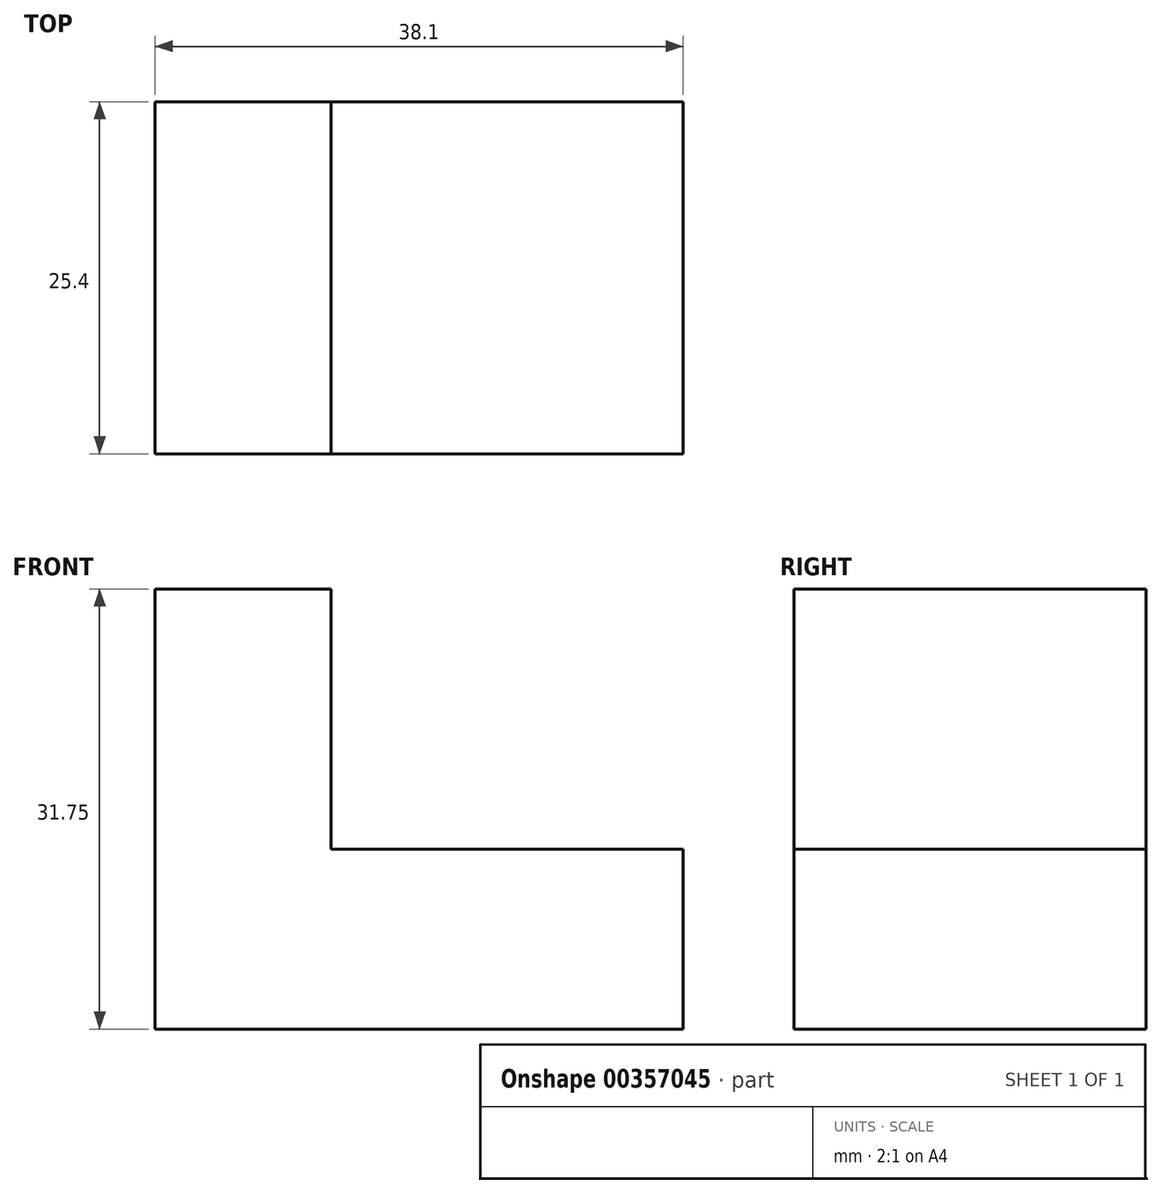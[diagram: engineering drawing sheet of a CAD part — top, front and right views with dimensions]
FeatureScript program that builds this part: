
annotation { "Feature Type Name" : "Feature", "Feature Type Description" : "" }
export const myFeature = defineFeature(function(context is Context, id is Id, definition is map)
    precondition{}
    {
        {
            var Q0;
            Q0=qCreatedBy(makeId("Front.planeOp"),FACE);
            var sketch = newSketch(context, id + "F0", { "sketchPlane" : qUnion([Q0])});
            skLineSegment(sketch, "E0", {"start": v(0, 0) * mm, "end": v(38.1, 0) * mm});
            skLineSegment(sketch, "E1", {"start": v(38.1, 0) * mm, "end": v(38.1, 12.97) * mm});
            skLineSegment(sketch, "E2", {"start": v(38.1, 12.97) * mm, "end": v(12.7, 12.97) * mm});
            skLineSegment(sketch, "E3", {"start": v(12.7, 12.97) * mm, "end": v(12.7, 31.75) * mm});
            skLineSegment(sketch, "E4", {"start": v(12.7, 31.75) * mm, "end": v(0, 31.75) * mm});
            skLineSegment(sketch, "E5", {"start": v(0, 31.75) * mm, "end": v(0, 0) * mm});
            skSolve(sketch);
        }
        {
            var Q0;
            Q0 = qSketchRegion(id + "F0", true);
            extrude(context, id + "F1", {"entities" : qUnion([Q0]), "depth" : 25.4 * mm});
        }
    });
